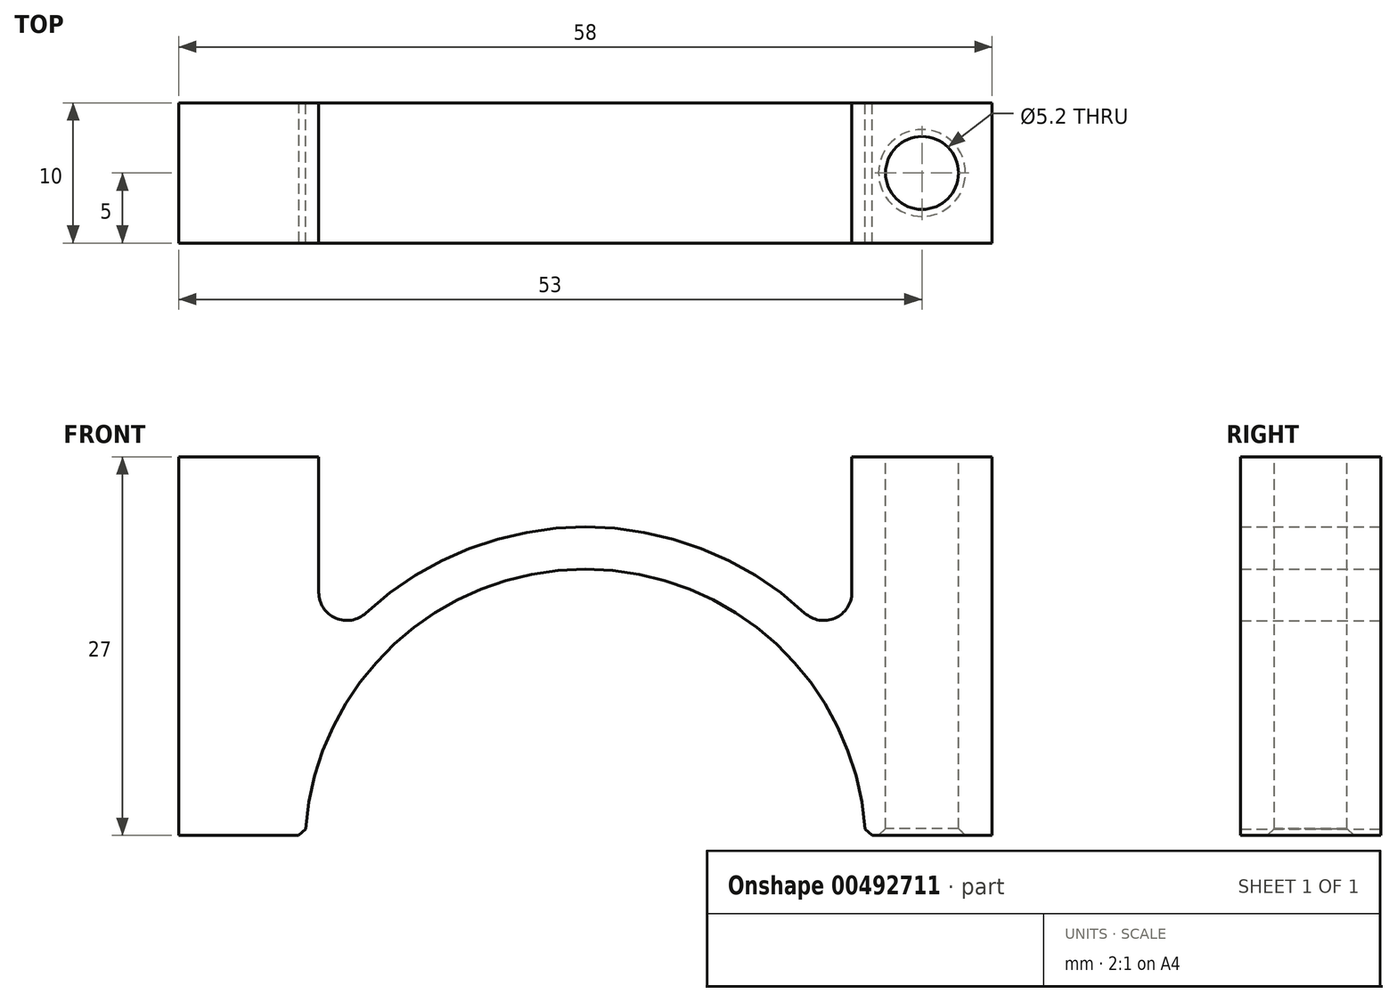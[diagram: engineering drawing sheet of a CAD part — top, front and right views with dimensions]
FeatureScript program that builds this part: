
annotation { "Feature Type Name" : "Feature", "Feature Type Description" : "" }
export const myFeature = defineFeature(function(context is Context, id is Id, definition is map)
    precondition{}
    {
        {
            var Q0;
            Q0=qCreatedBy(makeId("Front.planeOp"),FACE);
            var sketch = newSketch(context, id + "F0", { "sketchPlane" : qUnion([Q0])});
            skLineSegment(sketch, "E0", {"start": v(0, 91) * mm, "end": v(0, -41.9) * mm, "construction": true});
            skArc(sketch, "E1", {"start": v(19.97, 1) * mm, "mid": v(13.78, 14.5) * mm, "end": v(0, 20) * mm});
            skArc(sketch, "E2", {"start": v(15.64, 16.86) * mm, "mid": v(8.4, 21.41) * mm, "end": v(0, 23) * mm});
            skLineSegment(sketch, "E3", {"start": v(19.97, 1) * mm, "end": v(29, 1) * mm});
            skLineSegment(sketch, "E4", {"start": v(29, 1) * mm, "end": v(29, 28) * mm});
            skLineSegment(sketch, "E5", {"start": v(29, 28) * mm, "end": v(19, 28) * mm});
            skLineSegment(sketch, "E6", {"start": v(19, 28) * mm, "end": v(19, 18.33) * mm});
            skArc(sketch, "E7", {"start": v(15.64, 16.86) * mm, "mid": v(17.8, 16.5) * mm, "end": v(19, 18.33) * mm});
            skLineSegment(sketch, "E8.MirrorCS", {"start": v(-29, 1) * mm, "end": v(-29, 28) * mm});
            skLineSegment(sketch, "E9.MirrorCS", {"start": v(-29, 28) * mm, "end": v(-19, 28) * mm});
            skArc(sketch, "E10.MirrorCS", {"start": v(-15.64, 16.86) * mm, "mid": v(-8.4, 21.41) * mm, "end": v(0, 23) * mm});
            skLineSegment(sketch, "E11.MirrorCS", {"start": v(-19.97, 1) * mm, "end": v(-29, 1) * mm});
            skArc(sketch, "E12.MirrorCS", {"start": v(-19.97, 1) * mm, "mid": v(-13.78, 14.5) * mm, "end": v(0, 20) * mm});
            skArc(sketch, "E13.MirrorCS", {"start": v(-15.64, 16.86) * mm, "mid": v(-17.8, 16.5) * mm, "end": v(-19, 18.33) * mm});
            skLineSegment(sketch, "E14.MirrorCS", {"start": v(-19, 28) * mm, "end": v(-19, 18.33) * mm});
            skSolve(sketch);
        }
        {
            var Q0;
            Q0 = qSketchRegion(id + "F0", true);
            extrude(context, id + "F1", {"entities" : qUnion([Q0]), "endBound" : BoundingType.SYMMETRIC, "depth" : 10 * mm});
        }
        {
            var Q0;
            Q0=makeQuery(id+"F1.opExtrude","SWEPT_EDGE",EDGE,{"disambiguationData":[OSD([sQuery(id+"F0.wireOp",EDGE,"E1"),sQuery(id+"F0.wireOp",EDGE,"E3")])]});
            var Q1;
            Q1=makeQuery(id+"F1.opExtrude","SWEPT_EDGE",EDGE,{"disambiguationData":[OSD([sQuery(id+"F0.wireOp",EDGE,"E11.MirrorCS"),sQuery(id+"F0.wireOp",EDGE,"E12.MirrorCS")])]});
            chamfer(context, id + "F2", {"entities" : qUnion([Q0, Q1]), "width" : 0.5 * mm, "tangentPropagation" : true});
        }
        {
            var Q0;
            Q0=makeQuery(id+"F1.opExtrude","SWEPT_FACE",FACE,{"disambiguationData":[OSD([sQuery(id+"F0.wireOp",EDGE,"E5")])]});
            var sketch = newSketch(context, id + "F3", { "sketchPlane" : qUnion([Q0])});
            skCircle(sketch, "E15", {"center": v(24, 0) * mm, "radius": 2.6 * mm});
            skPoint(sketch, "E15.centerSnap0", {"position": v(29, 0) * mm});
            skLineSegment(sketch, "E16", {"start": v(0, 5) * mm, "end": v(0, -5) * mm, "construction": true});
            skSolve(sketch);
        }
        {
            var Q0;
            Q0 = qSketchRegion(id + "F3", true);
            extrude(context, id + "F4", {"entities" : qUnion([Q0]), "operationType" : NewBodyOperationType.REMOVE, "endBound" : BoundingType.THROUGH_ALL, "oppositeDirection" : true, "depth" : 25 * mm});
        }
        {
            var Q0;
            Q0=makeQuery(id+"F4.boolean.opBoolean","COPY",EDGE,{"derivedFrom":makeQuery(id+"F4.opExtrude","CAP_EDGE",EDGE,{"disambiguationData":[OSD([sQuery(id+"F3.wireOp",EDGE,"E15")])],"isStart":true})});
            var Q1;
            Q1=makeQuery(id+"F4.boolean.opBoolean","INTERSECT",EDGE,{"derivedFrom":[makeQuery(id+"F1.opExtrude","SWEPT_FACE",FACE,{"disambiguationData":[OSD([sQuery(id+"F0.wireOp",EDGE,"E3")])]}),makeQuery(id+"F4.opExtrude","SWEPT_FACE",FACE,{"disambiguationData":[OSD([sQuery(id+"F3.wireOp",EDGE,"E15")])]})]});
            chamfer(context, id + "F5", {"entities" : qUnion([Q0, Q1]), "width" : 0.5 * mm, "tangentPropagation" : true});
        }
    });
